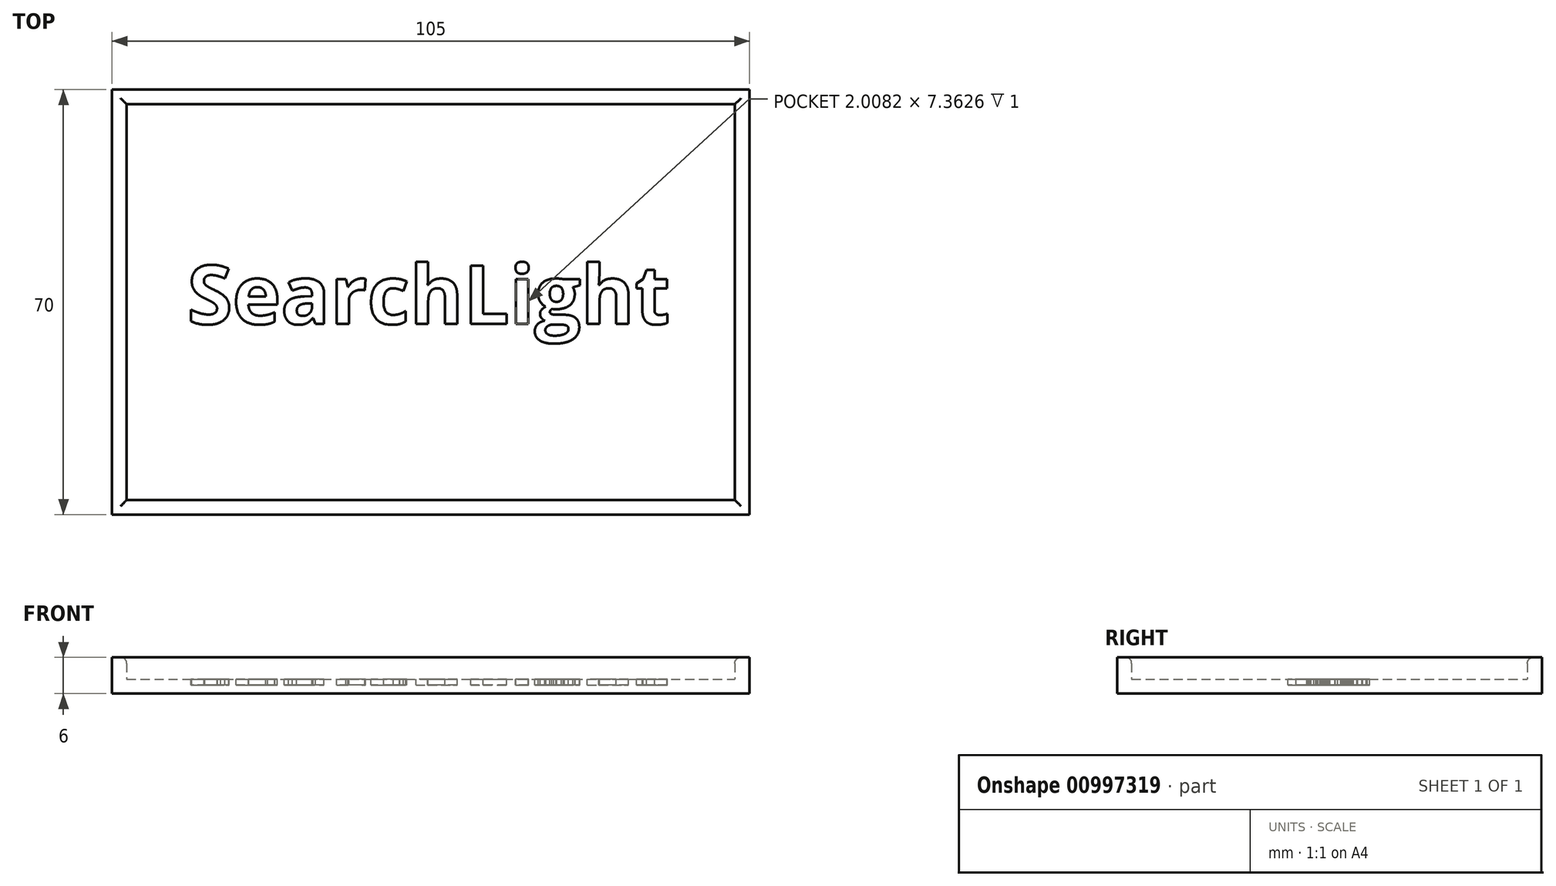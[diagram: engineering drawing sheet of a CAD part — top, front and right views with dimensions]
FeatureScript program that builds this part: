
annotation { "Feature Type Name" : "Feature", "Feature Type Description" : "" }
export const myFeature = defineFeature(function(context is Context, id is Id, definition is map)
    precondition{}
    {
        {
            var Q0;
            Q0=qCreatedBy(makeId("Top.planeOp"),FACE);
            var sketch = newSketch(context, id + "F0", { "sketchPlane" : qUnion([Q0])});
            skLineSegment(sketch, "E0.bottom", {"start": v(0, 0) * mm, "end": v(105, 0) * mm});
            skLineSegment(sketch, "E0.top", {"start": v(0, 70) * mm, "end": v(105, 70) * mm});
            skLineSegment(sketch, "E0.left", {"start": v(0, 0) * mm, "end": v(0, 70) * mm});
            skLineSegment(sketch, "E0.right", {"start": v(105, 0) * mm, "end": v(105, 70) * mm});
            skSolve(sketch);
        }
        {
            var Q0;
            Q0 = qSketchRegion(id + "F0", true);
            extrude(context, id + "F1", {"entities" : qUnion([Q0]), "depth" : 6 * mm, "offsetDistance" : 25 * mm});
        }
        {
            var Q0;
            Q0=makeQuery(id+"F1.opExtrude","CAP_FACE",FACE,{"disambiguationData":[OSD([sQuery(id+"F0.wireOp",EDGE,"E0.bottom"),sQuery(id+"F0.wireOp",EDGE,"E0.top"),sQuery(id+"F0.wireOp",EDGE,"E0.left"),sQuery(id+"F0.wireOp",EDGE,"E0.right")])],"isStart":false});
            shell(context, id + "F2", {"entities" : qUnion([Q0]), "thickness" : 2.4 * mm});
        }
        {
            var Q0;
            {var subQ0=sQuery(id+"F0.wireOp",EDGE,"E0.left");Q0=makeQuery(id+"F2.opShell","OFFSET_EDGE",EDGE,{"disambiguationData":[OSD([subQ0]),TDD([makeQuery(id+"F1.opExtrude","CAP_EDGE",EDGE,{"disambiguationData":[OSD([subQ0])],"isStart":false})])]});}
            var Q1;
            {var subQ0=sQuery(id+"F0.wireOp",EDGE,"E0.top");Q1=makeQuery(id+"F2.opShell","OFFSET_EDGE",EDGE,{"disambiguationData":[OSD([subQ0]),TDD([makeQuery(id+"F1.opExtrude","CAP_EDGE",EDGE,{"disambiguationData":[OSD([subQ0])],"isStart":false})])]});}
            var Q2;
            {var subQ0=sQuery(id+"F0.wireOp",EDGE,"E0.bottom");Q2=makeQuery(id+"F2.opShell","OFFSET_EDGE",EDGE,{"disambiguationData":[OSD([subQ0]),TDD([makeQuery(id+"F1.opExtrude","CAP_EDGE",EDGE,{"disambiguationData":[OSD([subQ0])],"isStart":false})])]});}
            var Q3;
            {var subQ0=sQuery(id+"F0.wireOp",EDGE,"E0.right");Q3=makeQuery(id+"F2.opShell","OFFSET_EDGE",EDGE,{"disambiguationData":[OSD([subQ0]),TDD([makeQuery(id+"F1.opExtrude","CAP_EDGE",EDGE,{"disambiguationData":[OSD([subQ0])],"isStart":false})])]});}
            fillet(context, id + "F3", {"entities" : qUnion([Q0, Q1, Q2, Q3]), "tangentPropagation" : true, "radius" : 1 * mm, "defaultsChanged" : true, "vertexSettings" : [], "allowEdgeOverflow" : false});
        }
        {
            var Q0;
            Q0=makeQuery(id+"F2.opShell","OFFSET_FACE",FACE,{"disambiguationData":[OSD([sQuery(id+"F0.wireOp",EDGE,"E0.bottom"),sQuery(id+"F0.wireOp",EDGE,"E0.top"),sQuery(id+"F0.wireOp",EDGE,"E0.left"),sQuery(id+"F0.wireOp",EDGE,"E0.right")])]});
            var sketch = newSketch(context, id + "F4", { "sketchPlane" : qUnion([Q0])});
            skText(sketch, "E1", { "text": "SearchLight", "fontName": "OpenSans-Bold.ttf"});
            const initialGuessF4  = {"E1": [0.0124, 0.0314, 1, 0, 0.00971]};
            skSetInitialGuess(sketch, initialGuessF4);
            skSolve(sketch);
        }
        {
            var Q0;
            Q0 = qSketchRegion(id + "F4", true);
            extrude(context, id + "F5", {"entities" : qUnion([Q0]), "operationType" : NewBodyOperationType.REMOVE, "depth" : -1 * mm, "offsetDistance" : 25 * mm});
        }
    });
